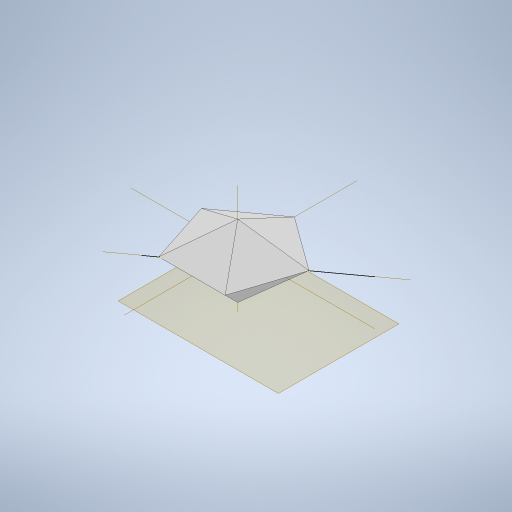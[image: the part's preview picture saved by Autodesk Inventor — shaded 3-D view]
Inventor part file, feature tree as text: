
AUTODESK INVENTOR PART (.ipt)
format: ipt  version: 2023 (Build 270158030, 158C)  size: 253,440 bytes
history: native  units: mm
features: sketch x3, plane x3, extrude x2, mirror x2, other x1, projected_geometry x1
ambient origin geometry x8: Origin, YZ Plane, XZ Plane, XY Plane, X Axis, Y Axis, Z Axis, Center Point
bodies: Body1 (feature_tree)
feature tree (12):
  extrude  "Extrusion2"  Depth=20.0mm
  sketch  "Sketch4"  dims[d18=20.0mm d19=-7.853982mm]
  other  "Work Axis6"
  extrude  "Extrusion3"  [1 undecoded]
  plane  "Work Plane3"
  mirror  "Mirror1"
  mirror  "Mirror2"
  plane  "Work Plane2"
  plane  "Work Plane1"
  sketch  "Sketch3"  dims[d15=40.0mm d16=20.0mm d17=-10.471976mm]
  sketch  "Sketch5"
  projected_geometry  "Projected Loop1"
note: 1 required parameter value undecoded (feature->parameter linkage not recoverable at this tier; creation-order binding heuristic only, values carry confidence <= 0.55)
